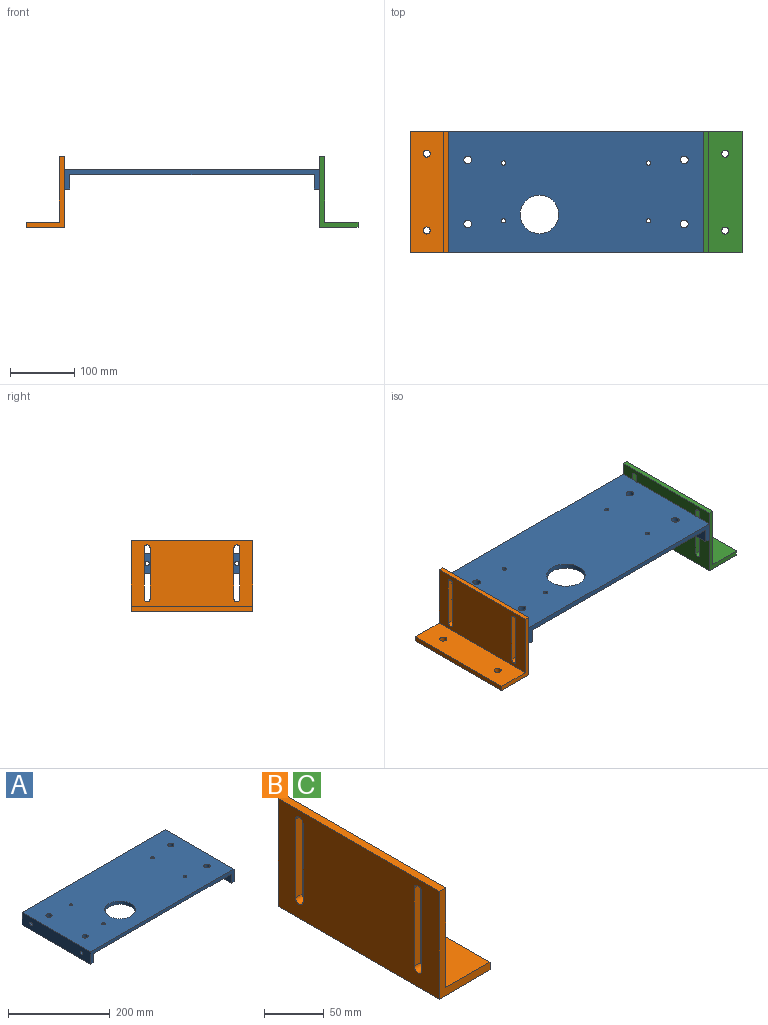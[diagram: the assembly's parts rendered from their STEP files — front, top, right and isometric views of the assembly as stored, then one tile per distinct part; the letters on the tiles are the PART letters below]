
ASSEMBLY  parts=3 mates=8
PART A: 23 faces, bbox 398x190x30 mm
  f0: plane 382x190mm, normal (0,0,-1), area 69154.9mm2, adj f2,f4,f6,f7,f8,f9,f11,f12
  f1: plane 190x30mm, normal (1,0,0), area 5627.4mm2, adj f2,f4,f5,f13,f20,f21
  f2: plane 398x30mm, normal (0,1,0), area 3536mm2, adj f0,f1,f3,f5,f10,f11,f12,f13
  f3: plane 190x30mm, normal (-1,0,0), area 5627.4mm2, adj f2,f4,f5,f10,f18,f19
  f4: plane 398x30mm, normal (0,-1,0), area 3536mm2, adj f0,f1,f3,f5,f10,f11,f12,f13
  f5: plane 398x190mm, normal (0,0,1), area 72194.9mm2, adj f1,f2,f3,f4,f6,f7,f8,f9
  f6: cylinder r=3.4mm len=8mm, axis (0,0,-1), area 170.9mm2, adj f0,f5
  f7: cylinder r=3.4mm len=8mm, axis (0,0,-1), area 170.9mm2, adj f0,f5
  f8: cylinder r=3.4mm len=8mm, axis (0,0,-1), area 170.9mm2, adj f0,f5
  f9: cylinder r=3.4mm len=8mm, axis (0,0,-1), area 170.9mm2, adj f0,f5
  f10: plane 190x8mm, normal (0,0,-1), area 1520mm2, adj f2,f3,f4,f11
  f11: plane 190x22mm, normal (1,0,0), area 4107.4mm2, adj f0,f2,f4,f10,f18,f19
  f12: plane 190x22mm, normal (-1,0,0), area 4107.4mm2, adj f0,f2,f4,f13,f20,f21
  f13: plane 190x8mm, normal (0,0,-1), area 1520mm2, adj f1,f2,f4,f12
  f14: cylinder r=6mm len=12mm, axis (0,0,1), area 301.6mm2, adj f0,f5
  f15: cylinder r=6mm len=12mm, axis (0,0,1), area 301.6mm2, adj f0,f5
  f16: cylinder r=6mm len=12mm, axis (0,0,1), area 301.6mm2, adj f0,f5
  f17: cylinder r=6mm len=12mm, axis (0,0,1), area 301.6mm2, adj f0,f5
  f18: cylinder r=3.4mm len=8mm, axis (-1,0,0), area 170.9mm2, adj f3,f11
  f19: cylinder r=3.4mm len=8mm, axis (-1,0,0), area 170.9mm2, adj f3,f11
  f20: cylinder r=3.4mm len=8mm, axis (1,0,0), area 170.9mm2, adj f1,f12
  f21: cylinder r=3.4mm len=8mm, axis (1,0,0), area 170.9mm2, adj f1,f12
  f22: cylinder r=30mm len=60mm, axis (0,0,1), area 1508mm2, adj f0,f5
PART B: 18 faces, bbox 60x190x110 mm
  f0: plane 190x8mm, normal (0,0,1), area 1520mm2, adj f1,f5,f6,f7
  f1: plane 190x110mm, normal (-1,0,0), area 19332.8mm2, adj f0,f2,f6,f7,f8,f9,f10,f11
  f2: plane 190x60mm, normal (0,0,-1), area 11209.9mm2, adj f1,f3,f6,f7,f16,f17
  f3: plane 190x8mm, normal (1,0,0), area 1520mm2, adj f2,f4,f6,f7
  f4: plane 190x52mm, normal (0,0,1), area 9689.9mm2, adj f3,f5,f6,f7,f16,f17
  f5: plane 190x102mm, normal (1,0,0), area 17812.8mm2, adj f0,f4,f6,f7,f8,f9,f10,f11
  f6: plane 110x60mm, normal (0,-1,0), area 1296mm2, adj f0,f1,f2,f3,f4,f5
  f7: plane 110x60mm, normal (0,1,0), area 1296mm2, adj f0,f1,f2,f3,f4,f5
  f8: plane 80x8mm, normal (0,-1,0), area 640mm2, adj f1,f5,f9,f11
  f9: cylinder r=4.5mm len=9mm, axis (1,0,0), area 113.1mm2, adj f1,f5,f8,f10
  f10: plane 80x8mm, normal (0,1,0), area 640mm2, adj f1,f5,f9,f11
  f11: cylinder r=4.5mm len=9mm, axis (1,0,0), area 113.1mm2, adj f1,f5,f8,f10
  f12: plane 80x8mm, normal (0,-1,0), area 640mm2, adj f1,f5,f13,f15
  f13: cylinder r=4.5mm len=9mm, axis (1,0,0), area 113.1mm2, adj f1,f5,f12,f14
  f14: plane 80x8mm, normal (0,1,0), area 640mm2, adj f1,f5,f13,f15
  f15: cylinder r=4.5mm len=9mm, axis (1,0,0), area 113.1mm2, adj f1,f5,f12,f14
  f16: cylinder r=5.5mm len=11mm, axis (0,0,1), area 276.5mm2, adj f2,f4
  f17: cylinder r=5.5mm len=11mm, axis (0,0,1), area 276.5mm2, adj f2,f4
PART C: same geometry as B
PLACE A t=(-88.06,-42.22,114.94)mm
PLACE B rot(axis=(0,0,1),180deg) t=(-287.06,-137.19,97.14)mm
PLACE C t=(110.94,52.75,97.14)mm
MATE parallel A.f2 <-> C.f7  axis (0,1,0) through (102.94,52.78,114.94)mm
MATE pin_slot C.f5 <-> C.f1  axis (1,0,0) through (118.94,32.25,92.27)mm
MATE parallel C.f1 <-> A.f1  axis (-1,0,0) through (110.94,-42.25,87.94)mm
MATE parallel C.f1 <-> A.f1  axis (-1,0,0) through (110.94,-42.25,87.94)mm
MATE parallel C.f2 <-> B.f2  axis (0,0,-1) through (140.87,-42.25,33.27)mm
MATE parallel A.f1 <-> C.f1  axis (1,0,0) through (110.94,-42.22,107.94)mm
MATE parallel C.f1 <-> A.f1  axis (-1,0,0) through (110.94,-42.25,87.94)mm
MATE parallel B.f1 <-> A.f3  axis (1,0,0) through (-287.06,-42.19,87.94)mm
